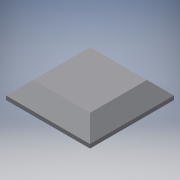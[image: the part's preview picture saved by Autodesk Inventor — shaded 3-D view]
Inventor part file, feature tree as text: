
AUTODESK INVENTOR PART (.ipt)
format: ipt  version: 2016 (Build 200138000, 138)  size: 92,160 bytes
history: native  units: mm
features: extrude x1, chamfer x1, sketch x1
ambient origin geometry x8: Origin, YZ Plane, XZ Plane, XY Plane, X Axis, Y Axis, Z Axis, Center Point
bodies: Solid1 (feature_tree)
feature tree (3):
  extrude  "Extrusion1"  Depth=43.5mm
  chamfer  "Chamfer1"  Distance=9.0mm
  sketch  "Sketch1"  dims[d0=43.5mm d1=43.5mm d2=9.0mm d3=0.0mm d4=7.0mm d5=2.0mm d6=45.0deg]
